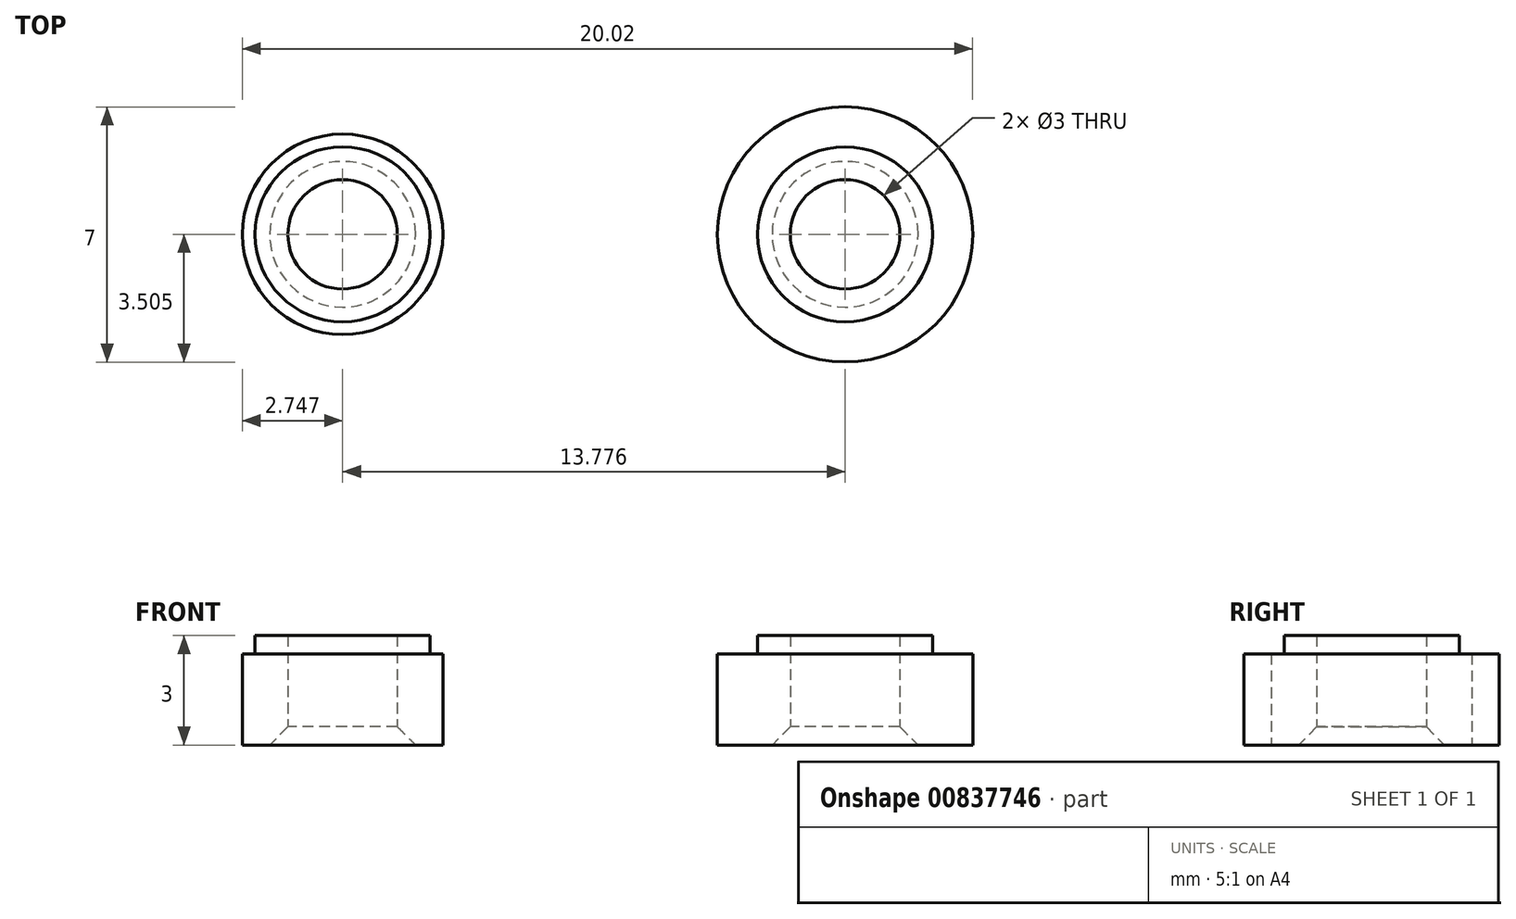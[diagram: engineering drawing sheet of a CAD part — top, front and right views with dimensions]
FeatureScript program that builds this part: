
annotation { "Feature Type Name" : "Feature", "Feature Type Description" : "" }
export const myFeature = defineFeature(function(context is Context, id is Id, definition is map)
    precondition{}
    {
        {
            var Q0;
            Q0=qCreatedBy(makeId("Top.planeOp"),FACE);
            var sketch = newSketch(context, id + "F0", { "sketchPlane" : qUnion([Q0])});
            skCircle(sketch, "E0", {"center": v(-30.86, 32.92) * mm, "radius": 1.5 * mm});
            skCircle(sketch, "E1", {"center": v(-30.86, 32.92) * mm, "radius": 2.4 * mm});
            skCircle(sketch, "E2", {"center": v(-17.09, 32.92) * mm, "radius": 1.5 * mm});
            skCircle(sketch, "E3", {"center": v(-17.09, 32.92) * mm, "radius": 2.4 * mm});
            skCircle(sketch, "E4", {"center": v(-17.09, 32.92) * mm, "radius": 3.5 * mm});
            skCircle(sketch, "E5", {"center": v(-30.86, 32.92) * mm, "radius": 2.75 * mm});
            skSolve(sketch);
        }
        {
            var Q0;
            Q0=makeQuery(id+"F0.imprint","IMPRINT",FACE,{"disambiguationData":[TD([[makeQuery(id+"F0.imprint","IMPRINT",EDGE,{"derivedFrom":sQuery(id+"F0.wireOp",EDGE,"E0")}),-1.0]])]});
            var Q1;
            Q1=makeQuery(id+"F0.imprint","IMPRINT",FACE,{"disambiguationData":[TD([[makeQuery(id+"F0.imprint","IMPRINT",EDGE,{"derivedFrom":sQuery(id+"F0.wireOp",EDGE,"E2")}),-1.0]])]});
            extrude(context, id + "F1", {"entities" : qUnion([Q0, Q1]), "depth" : 3 * mm, "offsetDistance" : 25 * mm});
        }
        {
            var Q0;
            Q0=makeQuery(id+"F0.imprint","IMPRINT",FACE,{"disambiguationData":[TD([[makeQuery(id+"F0.imprint","IMPRINT",EDGE,{"derivedFrom":sQuery(id+"F0.wireOp",EDGE,"E1")}),-1.0]])]});
            var Q1;
            Q1=makeQuery(id+"F0.imprint","IMPRINT",FACE,{"disambiguationData":[TD([[makeQuery(id+"F0.imprint","IMPRINT",EDGE,{"derivedFrom":sQuery(id+"F0.wireOp",EDGE,"E3")}),-1.0]])]});
            extrude(context, id + "F2", {"entities" : qUnion([Q0, Q1]), "operationType" : NewBodyOperationType.ADD, "depth" : 2.5 * mm, "offsetDistance" : 25 * mm});
        }
        {
            var Q0;
            Q0=makeQuery(id+"F1.opExtrude","CAP_EDGE",EDGE,{"disambiguationData":[OSD([sQuery(id+"F0.wireOp",EDGE,"E0")])],"isStart":true});
            var Q1;
            Q1=makeQuery(id+"F1.opExtrude","CAP_EDGE",EDGE,{"disambiguationData":[OSD([sQuery(id+"F0.wireOp",EDGE,"E2")])],"isStart":true});
            chamfer(context, id + "F3", {"entities" : qUnion([Q0, Q1]), "width" : 0.5 * mm, "tangentPropagation" : true});
        }
    });
